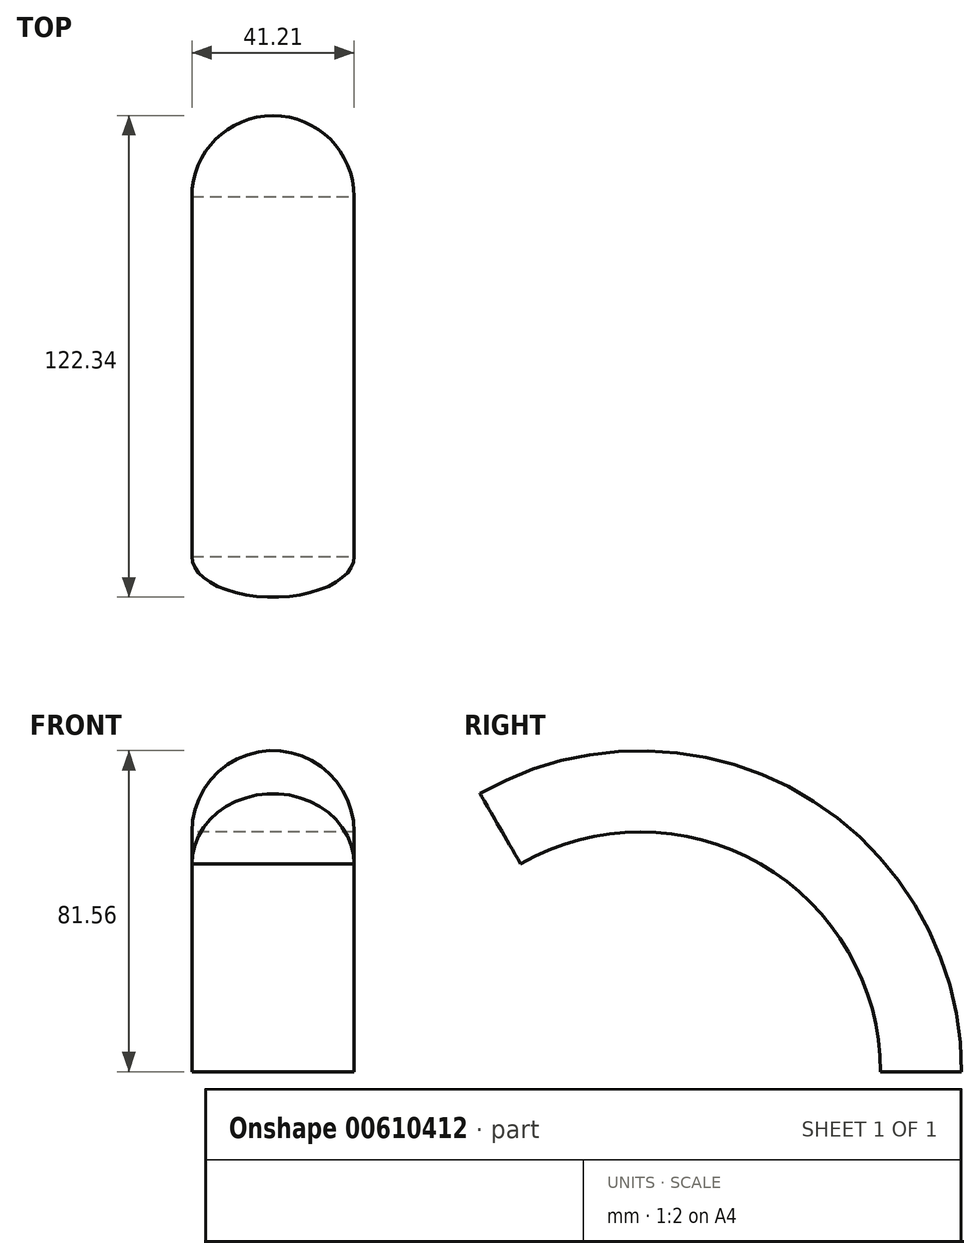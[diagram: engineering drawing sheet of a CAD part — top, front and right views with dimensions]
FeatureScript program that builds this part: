
annotation { "Feature Type Name" : "Feature", "Feature Type Description" : "" }
export const myFeature = defineFeature(function(context is Context, id is Id, definition is map)
    precondition{}
    {
        {
            var Q0;
            Q0=qCreatedBy(makeId("Top.planeOp"),FACE);
            var sketch = newSketch(context, id + "F0", { "sketchPlane" : qUnion([Q0])});
            skArc(sketch, "E0", {"start": v(41.2, 0) * mm, "mid": v(20.6, 20.6) * mm, "end": v(0, 0) * mm});
            skLineSegment(sketch, "E1", {"start": v(0, 0) * mm, "end": v(41.2, 0) * mm});
            skSolve(sketch);
        }
        {
            var Q0;
            Q0=qCreatedBy(makeId("Top.planeOp"),FACE);
            var sketch = newSketch(context, id + "F1", { "sketchPlane" : qUnion([Q0])});
            skLineSegment(sketch, "E2", {"start": v(-20.55, -60.96) * mm, "end": v(79.23, -60.96) * mm});
            skSolve(sketch);
        }
        {
            var Q0;
            Q0=makeQuery(id+"F0.imprint","IMPRINT",FACE,{"disambiguationData":[TD([[makeQuery(id+"F0.imprint","IMPRINT",EDGE,{"derivedFrom":sQuery(id+"F0.wireOp",EDGE,"E0")}),1.0]])]});
            var Q1;
            Q1=sQuery(id+"F1.wireOp",EDGE,"E2");
            revolve(context, id + "F2", {"entities" : qUnion([Q0]), "axis" : qUnion([Q1]), "revolveType" : RevolveType.ONE_DIRECTION, "angle" : 120 * degree});
        }
    });
